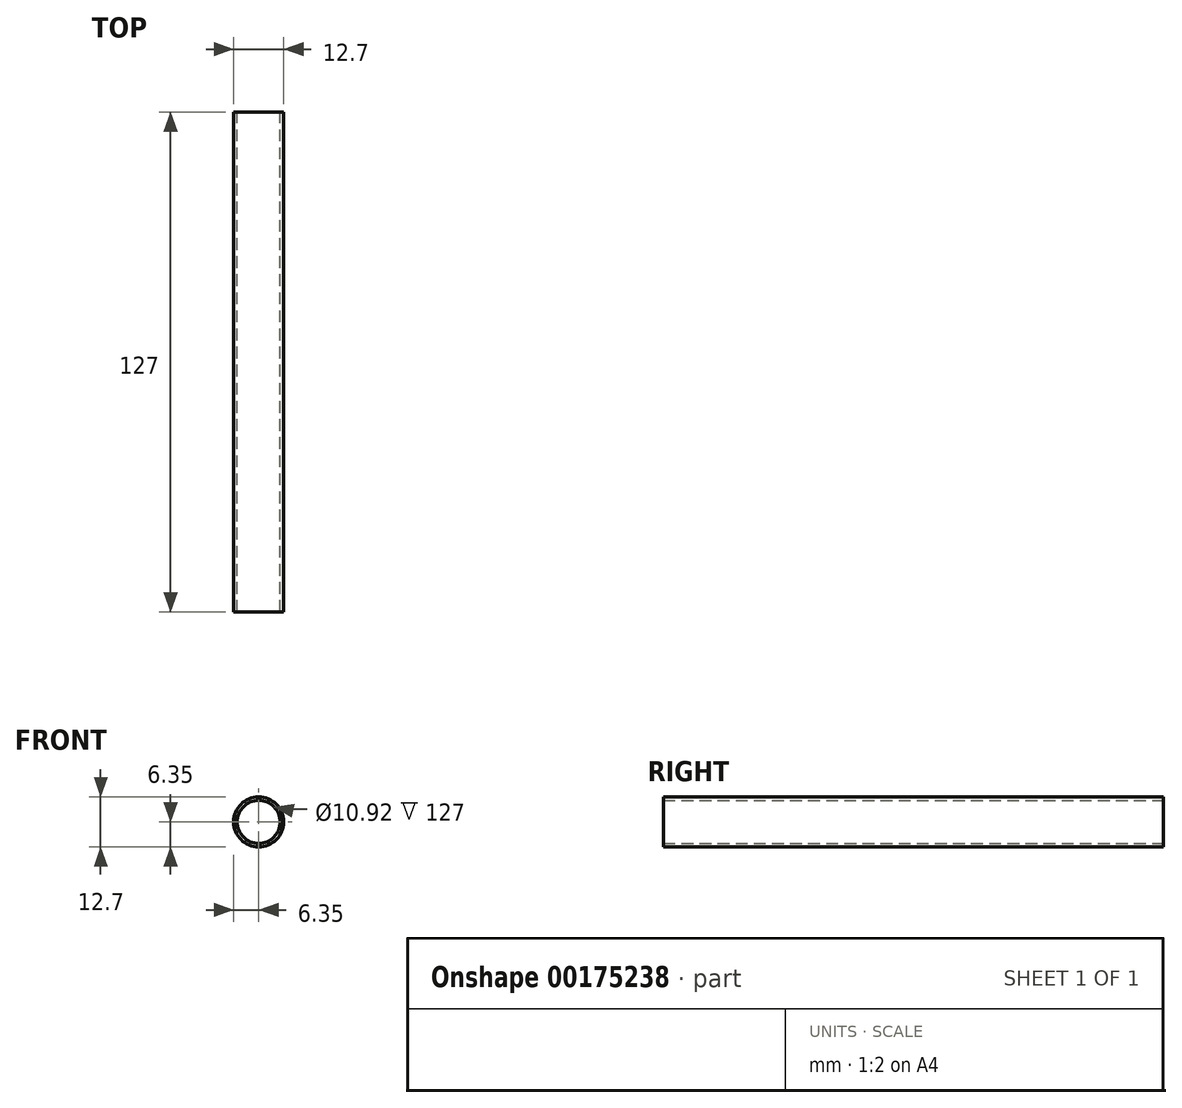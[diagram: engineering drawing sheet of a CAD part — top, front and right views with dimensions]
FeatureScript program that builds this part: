
annotation { "Feature Type Name" : "Feature", "Feature Type Description" : "" }
export const myFeature = defineFeature(function(context is Context, id is Id, definition is map)
    precondition{}
    {
        {
            var Q0;
            Q0=qCreatedBy(makeId("Front.planeOp"),FACE);
            var sketch = newSketch(context, id + "F0", { "sketchPlane" : qUnion([Q0])});
            skCircle(sketch, "E0", {"center": v(0, 0) * mm, "radius": 6.35 * mm});
            skCircle(sketch, "E1", {"center": v(0, 0) * mm, "radius": 5.46 * mm});
            skSolve(sketch);
        }
        {
            var Q0;
            Q0=makeQuery(id+"F0.imprint","IMPRINT",FACE,{"disambiguationData":[TD([[makeQuery(id+"F0.imprint","IMPRINT",EDGE,{"derivedFrom":sQuery(id+"F0.wireOp",EDGE,"E0")}),1.0]])]});
            extrude(context, id + "F1", {"entities" : qUnion([Q0]), "depth" : 127 * mm});
        }
    });
